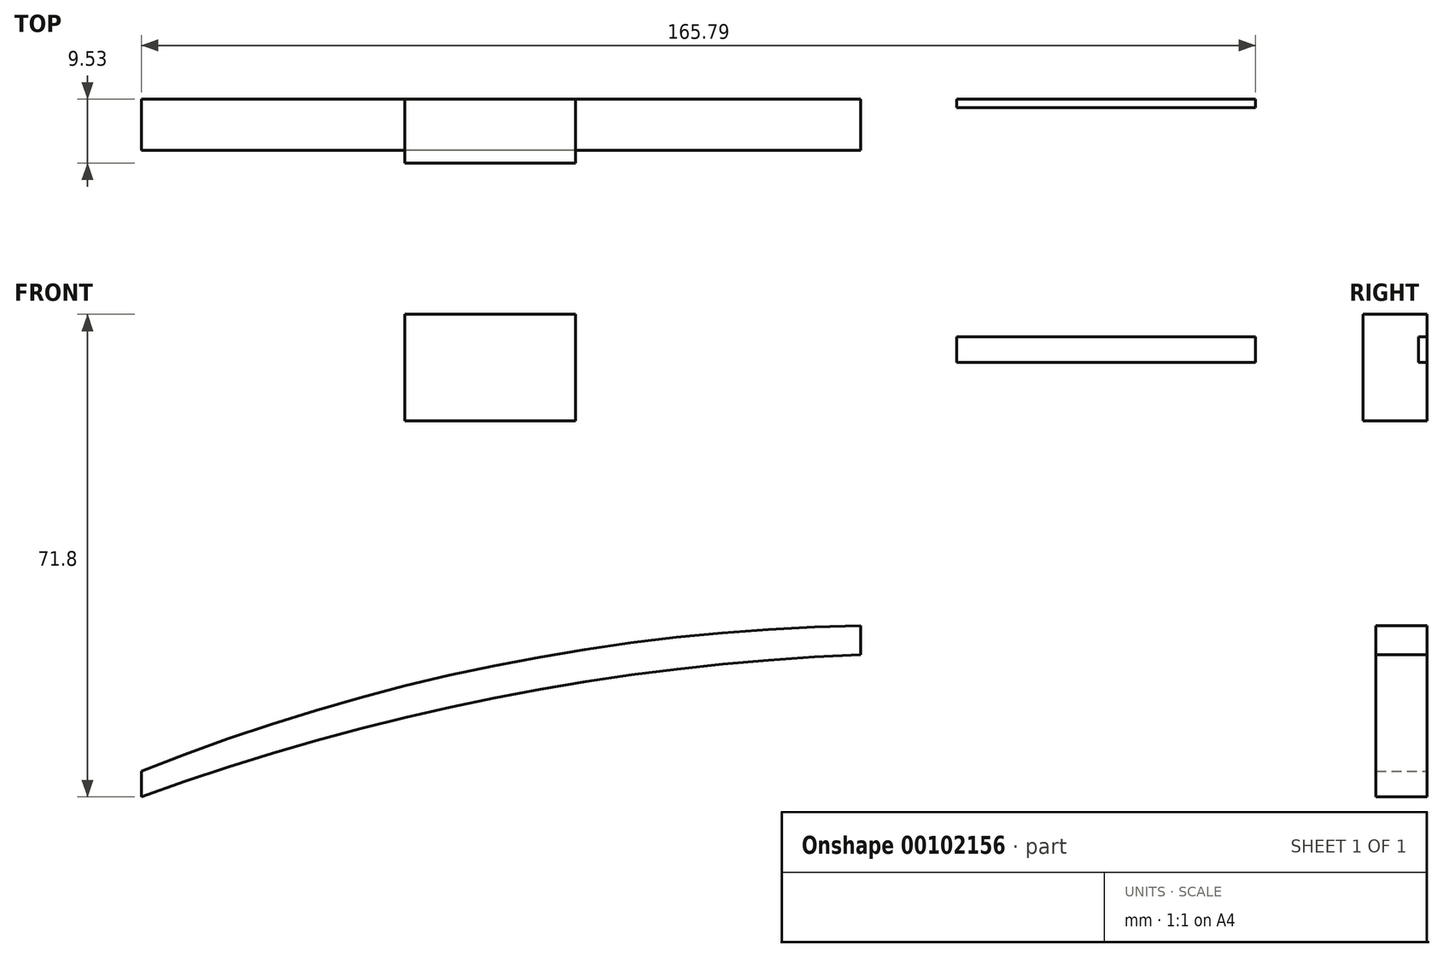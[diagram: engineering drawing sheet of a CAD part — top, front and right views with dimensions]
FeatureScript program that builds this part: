
annotation { "Feature Type Name" : "Feature", "Feature Type Description" : "" }
export const myFeature = defineFeature(function(context is Context, id is Id, definition is map)
    precondition{}
    {
        {
            var Q0;
            Q0=qCreatedBy(makeId("Front.planeOp"),FACE);
            var sketch = newSketch(context, id + "F0", { "sketchPlane" : qUnion([Q0])});
            skLineSegment(sketch, "E0.bottom", {"start": v(-55.64, 32.83) * mm, "end": v(-30.24, 32.83) * mm});
            skLineSegment(sketch, "E0.top", {"start": v(-55.64, 16.96) * mm, "end": v(-30.24, 16.96) * mm});
            skLineSegment(sketch, "E0.left", {"start": v(-55.64, 32.83) * mm, "end": v(-55.64, 16.96) * mm});
            skLineSegment(sketch, "E0.right", {"start": v(-30.24, 32.83) * mm, "end": v(-30.24, 16.96) * mm});
            skSolve(sketch);
        }
        {
            var Q0;
            Q0 = qSketchRegion(id + "F0", true);
            extrude(context, id + "F1", {"entities" : qUnion([Q0]), "depth" : 9.52 * mm});
        }
        {
            var Q0;
            Q0=qCreatedBy(makeId("Front.planeOp"),FACE);
            var sketch = newSketch(context, id + "F2", { "sketchPlane" : qUnion([Q0])});
            skLineSegment(sketch, "E1.bottom", {"start": v(26.5, 29.5) * mm, "end": v(70.94, 29.5) * mm});
            skLineSegment(sketch, "E1.top", {"start": v(26.5, 25.7) * mm, "end": v(70.94, 25.7) * mm});
            skLineSegment(sketch, "E1.left", {"start": v(26.5, 29.5) * mm, "end": v(26.5, 25.7) * mm});
            skLineSegment(sketch, "E1.right", {"start": v(70.94, 29.5) * mm, "end": v(70.94, 25.7) * mm});
            skSolve(sketch);
        }
        {
            var Q0;
            Q0 = qSketchRegion(id + "F2", true);
            extrude(context, id + "F3", {"entities" : qUnion([Q0]), "depth" : 1.27 * mm});
        }
        {
            var Q0;
            Q0=qCreatedBy(makeId("Front.planeOp"),FACE);
            var sketch = newSketch(context, id + "F4", { "sketchPlane" : qUnion([Q0])});
            skLineSegment(sketch, "E2", {"start": v(-94.85, -38.97) * mm, "end": v(-94.85, -35.16) * mm});
            skLineSegment(sketch, "E3", {"start": v(12.18, -13.5) * mm, "end": v(12.18, -17.8) * mm});
            skArc(sketch, "E4.trimOffspring", {"start": v(12.18, -13.5) * mm, "mid": v(-42.32, -19.46) * mm, "end": v(-94.85, -35.16) * mm});
            skArc(sketch, "E5", {"start": v(12.18, -17.8) * mm, "mid": v(-42.16, -24.23) * mm, "end": v(-94.85, -38.97) * mm});
            skSolve(sketch);
        }
        {
            var Q0;
            Q0 = qSketchRegion(id + "F4", true);
            extrude(context, id + "F5", {"entities" : qUnion([Q0]), "depth" : 7.62 * mm});
        }
    });
